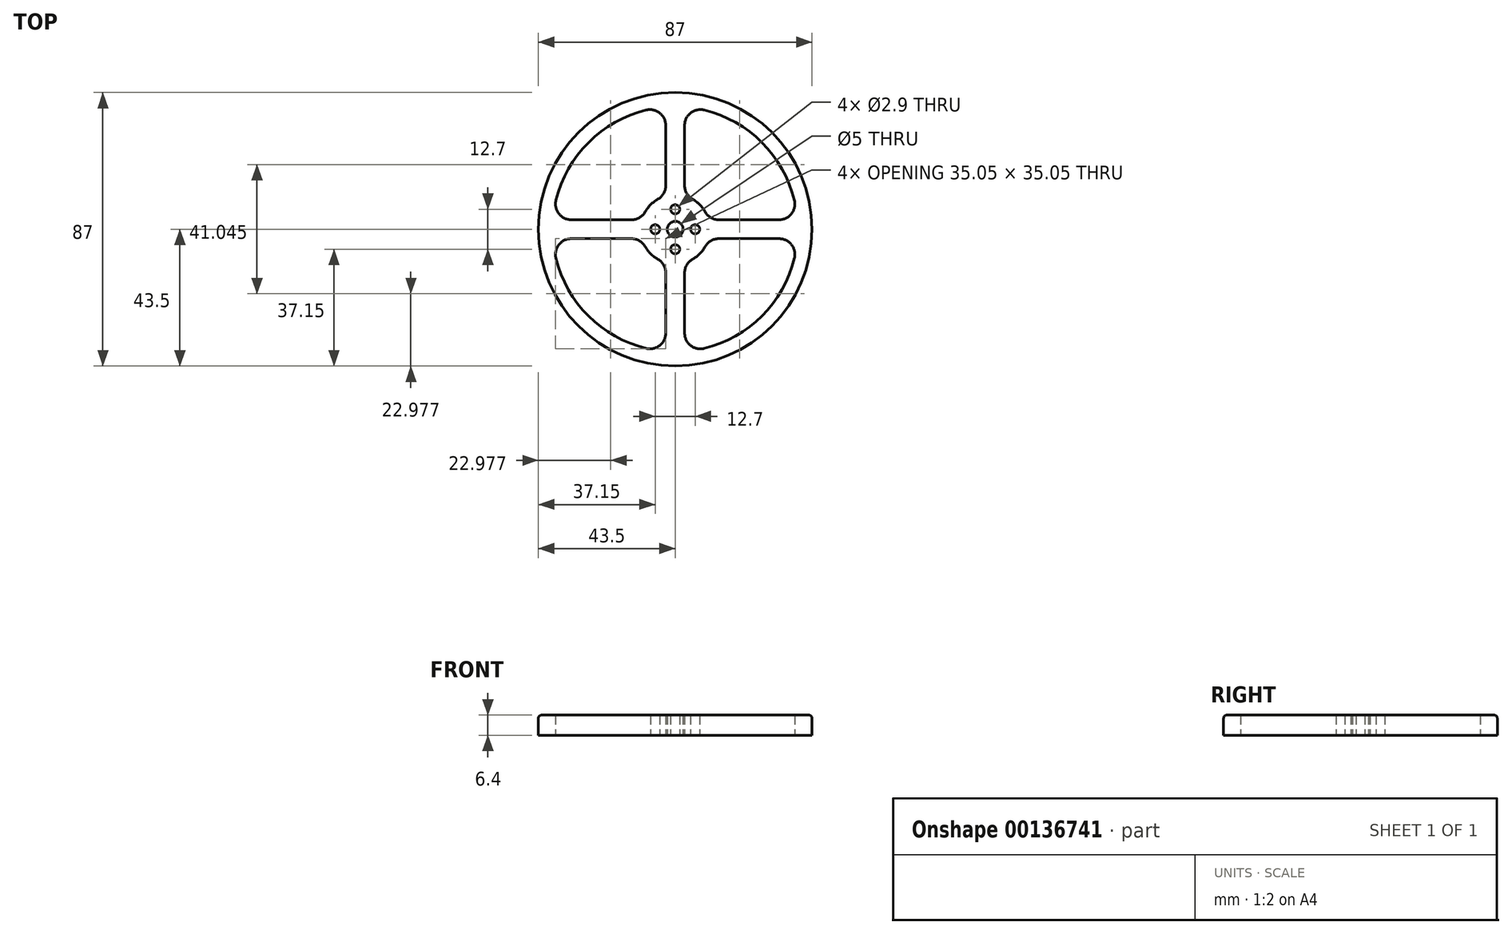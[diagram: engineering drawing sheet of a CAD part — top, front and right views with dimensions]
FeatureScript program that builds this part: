
annotation { "Feature Type Name" : "Feature", "Feature Type Description" : "" }
export const myFeature = defineFeature(function(context is Context, id is Id, definition is map)
    precondition{}
    {
        {
            var Q0;
            Q0=qCreatedBy(makeId("Top.planeOp"),FACE);
            var sketch = newSketch(context, id + "F0", { "sketchPlane" : qUnion([Q0])});
            skCircle(sketch, "E0", {"center": v(0, 0) * mm, "radius": 2.5 * mm});
            skCircle(sketch, "E1", {"center": v(-6.35, 0) * mm, "radius": 1.45 * mm});
            skCircle(sketch, "E2.1.0", {"center": v(0, 6.35) * mm, "radius": 1.45 * mm});
            skCircle(sketch, "E2.2.0", {"center": v(6.35, 0) * mm, "radius": 1.45 * mm});
            skCircle(sketch, "E2.3.0", {"center": v(0, -6.35) * mm, "radius": 1.45 * mm});
            skLineSegment(sketch, "E2.anchor1", {"start": v(0, 0) * mm, "end": v(-6.35, 0) * mm, "construction": true});
            skLineSegment(sketch, "E2.anchor2", {"start": v(0, 0) * mm, "end": v(0, -6.35) * mm, "construction": true});
            skLineSegment(sketch, "E3", {"start": v(0, 0) * mm, "end": v(0, 8.03) * mm, "construction": true});
            skLineSegment(sketch, "E4", {"start": v(0, 0) * mm, "end": v(8.03, 0) * mm, "construction": true});
            skArc(sketch, "E5", {"start": v(0, 8.03) * mm, "mid": v(-5.67, -5.67) * mm, "end": v(8.03, 0) * mm, "construction": true});
            skArc(sketch, "E6", {"start": v(8.03, 0) * mm, "mid": v(5.67, 5.67) * mm, "end": v(0, 8.03) * mm, "construction": true});
            skLineSegment(sketch, "E7", {"start": v(0, 8.03) * mm, "end": v(0, 42) * mm, "construction": true});
            skLineSegment(sketch, "E8", {"start": v(8.03, 0) * mm, "end": v(42, 0) * mm, "construction": true});
            skLineSegment(sketch, "E9", {"start": v(0, 42) * mm, "end": v(0, 42) * mm});
            skArc(sketch, "E10", {"start": v(0, 42) * mm, "mid": v(-29.7, -29.7) * mm, "end": v(42, 0) * mm, "construction": true});
            skArc(sketch, "E11", {"start": v(42, 0) * mm, "mid": v(29.7, 29.7) * mm, "end": v(0, 42) * mm, "construction": true});
            skLineSegment(sketch, "E12.0", {"start": v(3, 10.6) * mm, "end": v(3, 38.88) * mm});
            skArc(sketch, "E12.1", {"start": v(10.6, 3) * mm, "mid": v(7.8, 7.8) * mm, "end": v(3, 10.6) * mm});
            skLineSegment(sketch, "E12.2", {"start": v(10.6, 3) * mm, "end": v(38.88, 3) * mm});
            skArc(sketch, "E12.3", {"start": v(38.88, 3) * mm, "mid": v(27.58, 27.58) * mm, "end": v(3, 38.88) * mm});
            skLineSegment(sketch, "E13.1.0", {"start": v(10.6, -3) * mm, "end": v(38.88, -3) * mm});
            skArc(sketch, "E13.1.1", {"start": v(3, -10.6) * mm, "mid": v(7.8, -7.8) * mm, "end": v(10.6, -3) * mm});
            skLineSegment(sketch, "E13.1.2", {"start": v(3, -10.6) * mm, "end": v(3, -38.88) * mm});
            skArc(sketch, "E13.1.3", {"start": v(3, -38.88) * mm, "mid": v(27.58, -27.58) * mm, "end": v(38.88, -3) * mm});
            skLineSegment(sketch, "E13.2.0", {"start": v(-3, -10.6) * mm, "end": v(-3, -38.88) * mm});
            skArc(sketch, "E13.2.1", {"start": v(-10.6, -3) * mm, "mid": v(-7.8, -7.8) * mm, "end": v(-3, -10.6) * mm});
            skLineSegment(sketch, "E13.2.2", {"start": v(-10.6, -3) * mm, "end": v(-38.88, -3) * mm});
            skArc(sketch, "E13.2.3", {"start": v(-38.88, -3) * mm, "mid": v(-27.58, -27.58) * mm, "end": v(-3, -38.88) * mm});
            skLineSegment(sketch, "E13.3.0", {"start": v(-10.6, 3) * mm, "end": v(-38.88, 3) * mm});
            skArc(sketch, "E13.3.1", {"start": v(-3, 10.6) * mm, "mid": v(-7.8, 7.8) * mm, "end": v(-10.6, 3) * mm});
            skLineSegment(sketch, "E13.3.2", {"start": v(-3, 10.6) * mm, "end": v(-3, 38.88) * mm});
            skArc(sketch, "E13.3.3", {"start": v(-3, 38.88) * mm, "mid": v(-27.58, 27.58) * mm, "end": v(-38.88, 3) * mm});
            skLineSegment(sketch, "E13.anchor1", {"start": v(0, 0) * mm, "end": v(3, 10.6) * mm, "construction": true});
            skLineSegment(sketch, "E13.anchor2", {"start": v(0, 0) * mm, "end": v(-10.6, 3) * mm, "construction": true});
            skCircle(sketch, "E14", {"center": v(0, 0) * mm, "radius": 43.5 * mm});
            skSolve(sketch);
        }
        {
            var Q0;
            Q0=makeQuery(id+"F0.imprint","IMPRINT",FACE,{"disambiguationData":[TD([[makeQuery(id+"F0.imprint","IMPRINT",EDGE,{"derivedFrom":sQuery(id+"F0.wireOp",EDGE,"E0")}),-1.0]])]});
            extrude(context, id + "F1", {"entities" : qUnion([Q0]), "depth" : 6.4 * mm, "offsetDistance" : 25 * mm});
        }
        {
            var Q0;
            Q0=makeQuery(id+"F1.opExtrude","SWEPT_EDGE",EDGE,{"disambiguationData":[OSD([sQuery(id+"F0.wireOp",EDGE,"E13.2.1"),sQuery(id+"F0.wireOp",EDGE,"E13.2.2")])]});
            var Q1;
            Q1=makeQuery(id+"F1.opExtrude","SWEPT_EDGE",EDGE,{"disambiguationData":[OSD([sQuery(id+"F0.wireOp",EDGE,"E13.2.0"),sQuery(id+"F0.wireOp",EDGE,"E13.2.1")])]});
            var Q2;
            Q2=makeQuery(id+"F1.opExtrude","SWEPT_EDGE",EDGE,{"disambiguationData":[OSD([sQuery(id+"F0.wireOp",EDGE,"E13.3.1"),sQuery(id+"F0.wireOp",EDGE,"E13.3.2")])]});
            var Q3;
            Q3=makeQuery(id+"F1.opExtrude","SWEPT_EDGE",EDGE,{"disambiguationData":[OSD([sQuery(id+"F0.wireOp",EDGE,"E13.3.0"),sQuery(id+"F0.wireOp",EDGE,"E13.3.1")])]});
            var Q4;
            Q4=makeQuery(id+"F1.opExtrude","SWEPT_EDGE",EDGE,{"disambiguationData":[OSD([sQuery(id+"F0.wireOp",EDGE,"E13.1.1"),sQuery(id+"F0.wireOp",EDGE,"E13.1.2")])]});
            var Q5;
            Q5=makeQuery(id+"F1.opExtrude","SWEPT_EDGE",EDGE,{"disambiguationData":[OSD([sQuery(id+"F0.wireOp",EDGE,"E13.1.0"),sQuery(id+"F0.wireOp",EDGE,"E13.1.1")])]});
            var Q6;
            Q6=makeQuery(id+"F1.opExtrude","SWEPT_EDGE",EDGE,{"disambiguationData":[OSD([sQuery(id+"F0.wireOp",EDGE,"E12.1"),sQuery(id+"F0.wireOp",EDGE,"E12.2")])]});
            var Q7;
            Q7=makeQuery(id+"F1.opExtrude","SWEPT_EDGE",EDGE,{"disambiguationData":[OSD([sQuery(id+"F0.wireOp",EDGE,"E12.0"),sQuery(id+"F0.wireOp",EDGE,"E12.1")])]});
            var Q8;
            Q8=makeQuery(id+"F1.opExtrude","SWEPT_EDGE",EDGE,{"disambiguationData":[OSD([sQuery(id+"F0.wireOp",EDGE,"E13.2.2"),sQuery(id+"F0.wireOp",EDGE,"E13.2.3")])]});
            var Q9;
            Q9=makeQuery(id+"F1.opExtrude","SWEPT_EDGE",EDGE,{"disambiguationData":[OSD([sQuery(id+"F0.wireOp",EDGE,"E13.2.0"),sQuery(id+"F0.wireOp",EDGE,"E13.2.3")])]});
            var Q10;
            Q10=makeQuery(id+"F1.opExtrude","SWEPT_EDGE",EDGE,{"disambiguationData":[OSD([sQuery(id+"F0.wireOp",EDGE,"E13.1.2"),sQuery(id+"F0.wireOp",EDGE,"E13.1.3")])]});
            var Q11;
            Q11=makeQuery(id+"F1.opExtrude","SWEPT_EDGE",EDGE,{"disambiguationData":[OSD([sQuery(id+"F0.wireOp",EDGE,"E13.1.0"),sQuery(id+"F0.wireOp",EDGE,"E13.1.3")])]});
            var Q12;
            Q12=makeQuery(id+"F1.opExtrude","SWEPT_EDGE",EDGE,{"disambiguationData":[OSD([sQuery(id+"F0.wireOp",EDGE,"E12.2"),sQuery(id+"F0.wireOp",EDGE,"E12.3")])]});
            var Q13;
            Q13=makeQuery(id+"F1.opExtrude","SWEPT_EDGE",EDGE,{"disambiguationData":[OSD([sQuery(id+"F0.wireOp",EDGE,"E12.0"),sQuery(id+"F0.wireOp",EDGE,"E12.3")])]});
            var Q14;
            Q14=makeQuery(id+"F1.opExtrude","SWEPT_EDGE",EDGE,{"disambiguationData":[OSD([sQuery(id+"F0.wireOp",EDGE,"E13.3.2"),sQuery(id+"F0.wireOp",EDGE,"E13.3.3")])]});
            var Q15;
            Q15=makeQuery(id+"F1.opExtrude","SWEPT_EDGE",EDGE,{"disambiguationData":[OSD([sQuery(id+"F0.wireOp",EDGE,"E13.3.0"),sQuery(id+"F0.wireOp",EDGE,"E13.3.3")])]});
            fillet(context, id + "F2", {"entities" : qUnion([Q0, Q1, Q2, Q3, Q4, Q5, Q6, Q7, Q8, Q9, Q10, Q11, Q12, Q13, Q14, Q15]), "radius" : 5 * mm, "tangentPropagation" : true, "allowEdgeOverflow" : false});
        }
        {
            var Q0;
            Q0=makeQuery(id+"F1.opExtrude","CAP_EDGE",EDGE,{"disambiguationData":[OSD([sQuery(id+"F0.wireOp",EDGE,"E14")])],"isStart":false});
            fillet(context, id + "F3", {"entities" : qUnion([Q0]), "radius" : 1 * mm, "tangentPropagation" : true, "allowEdgeOverflow" : false});
        }
    });
